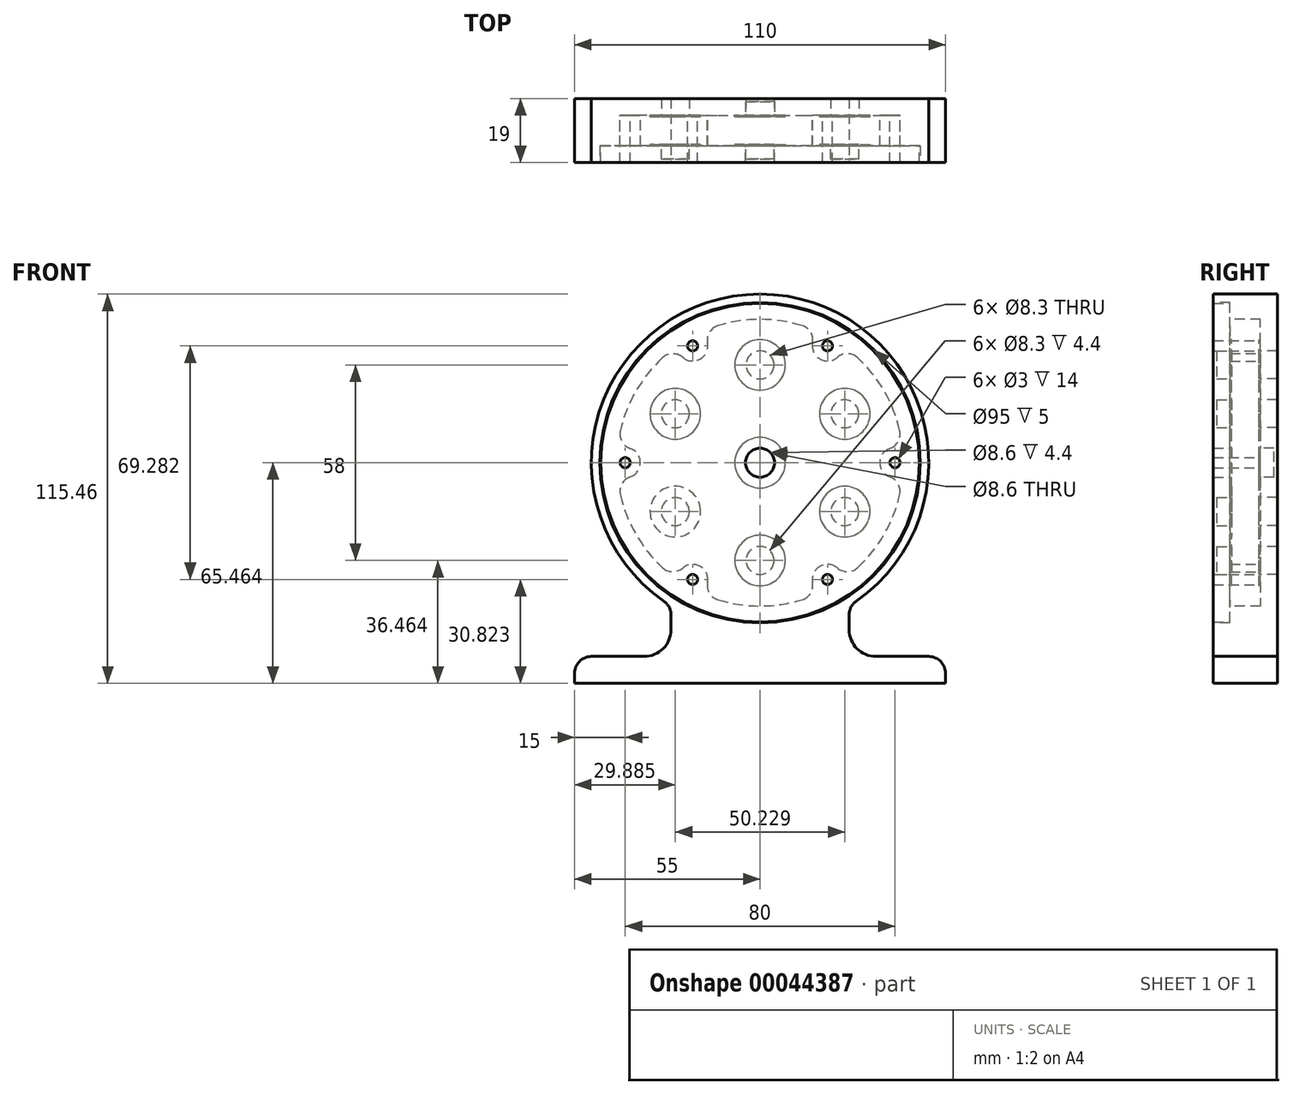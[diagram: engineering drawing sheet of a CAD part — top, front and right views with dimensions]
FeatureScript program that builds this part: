
annotation { "Feature Type Name" : "Feature", "Feature Type Description" : "" }
export const myFeature = defineFeature(function(context is Context, id is Id, definition is map)
    precondition{}
    {
        {
            var Q0;
            Q0=qCreatedBy(makeId("Front.planeOp"),FACE);
            var sketch = newSketch(context, id + "F0", { "sketchPlane" : qUnion([Q0])});
            skLineSegment(sketch, "E0", {"start": v(0, 0) * mm, "end": v(-55, 0) * mm});
            skLineSegment(sketch, "E1", {"start": v(-55, 0) * mm, "end": v(-55, 3) * mm});
            skLineSegment(sketch, "E2", {"start": v(-50, 8) * mm, "end": v(-34.4, 8) * mm});
            skLineSegment(sketch, "E3", {"start": v(-26.4, 16) * mm, "end": v(-26.4, 20.3) * mm});
            skArc(sketch, "E4", {"start": v(28.54, 24.41) * mm, "mid": v(0, 115.46) * mm, "end": v(-28.54, 24.41) * mm});
            skLineSegment(sketch, "E5", {"start": v(0, 65.46) * mm, "end": v(0, 0) * mm, "construction": true});
            skLineSegment(sketch, "E6.MirrorCS", {"start": v(0, 0) * mm, "end": v(55, 0) * mm});
            skLineSegment(sketch, "E7.MirrorCS", {"start": v(55, 0) * mm, "end": v(55, 3) * mm});
            skLineSegment(sketch, "E8.MirrorCS", {"start": v(50, 8) * mm, "end": v(34.4, 8) * mm});
            skLineSegment(sketch, "E9.MirrorCS", {"start": v(26.4, 16) * mm, "end": v(26.4, 20.3) * mm});
            skPoint(sketch, "E10.visualSharp", {"position": v(-55, 8) * mm});
            skArc(sketch, "E10.filletArc", {"start": v(-50, 8) * mm, "mid": v(-53.54, 6.54) * mm, "end": v(-55, 3) * mm});
            skPoint(sketch, "E11.visualSharp", {"position": v(55, 8) * mm});
            skArc(sketch, "E11.filletArc", {"start": v(55, 3) * mm, "mid": v(53.54, 6.54) * mm, "end": v(50, 8) * mm});
            skPoint(sketch, "E12.visualSharp", {"position": v(-26.4, 8) * mm});
            skArc(sketch, "E12.filletArc", {"start": v(-34.4, 8) * mm, "mid": v(-28.74, 10.34) * mm, "end": v(-26.4, 16) * mm});
            skPoint(sketch, "E13.visualSharp", {"position": v(26.4, 8) * mm});
            skArc(sketch, "E13.filletArc", {"start": v(26.4, 16) * mm, "mid": v(28.74, 10.34) * mm, "end": v(34.4, 8) * mm});
            skPoint(sketch, "E14.visualSharp", {"position": v(26.4, 23) * mm});
            skArc(sketch, "E14.filletArc", {"start": v(28.54, 24.41) * mm, "mid": v(26.97, 22.62) * mm, "end": v(26.4, 20.3) * mm});
            skPoint(sketch, "E15.visualSharp", {"position": v(-26.4, 23) * mm});
            skArc(sketch, "E15.filletArc", {"start": v(-26.4, 20.3) * mm, "mid": v(-26.97, 22.62) * mm, "end": v(-28.54, 24.41) * mm});
            skSolve(sketch);
        }
        {
            var Q0;
            Q0=makeQuery(id+"F0.imprint","IMPRINT",FACE,{"disambiguationData":[TD([[makeQuery(id+"F0.imprint","IMPRINT",EDGE,{"derivedFrom":sQuery(id+"F0.wireOp",EDGE,"E0")}),-1.0]])]});
            extrude(context, id + "F1", {"entities" : qUnion([Q0]), "oppositeDirection" : true, "depth" : 19 * mm});
        }
        {
            var Q0;
            Q0=makeQuery(id+"F1.opExtrude","CAP_FACE",FACE,{"disambiguationData":[OSD([sQuery(id+"F0.wireOp",EDGE,"E0"),sQuery(id+"F0.wireOp",EDGE,"E1"),sQuery(id+"F0.wireOp",EDGE,"E2"),sQuery(id+"F0.wireOp",EDGE,"E3"),sQuery(id+"F0.wireOp",EDGE,"E4"),sQuery(id+"F0.wireOp",EDGE,"E6.MirrorCS"),sQuery(id+"F0.wireOp",EDGE,"E7.MirrorCS"),sQuery(id+"F0.wireOp",EDGE,"E8.MirrorCS"),sQuery(id+"F0.wireOp",EDGE,"E9.MirrorCS"),sQuery(id+"F0.wireOp",EDGE,"E10.filletArc"),sQuery(id+"F0.wireOp",EDGE,"E11.filletArc"),sQuery(id+"F0.wireOp",EDGE,"E12.filletArc"),sQuery(id+"F0.wireOp",EDGE,"E13.filletArc"),sQuery(id+"F0.wireOp",EDGE,"E14.filletArc"),sQuery(id+"F0.wireOp",EDGE,"E15.filletArc")])],"isStart":true});
            var sketch = newSketch(context, id + "F2", { "sketchPlane" : qUnion([Q0])});
            skCircle(sketch, "E16", {"center": v(0, 65.46) * mm, "radius": 47.5 * mm});
            skSolve(sketch);
        }
        {
            var Q0;
            Q0=makeQuery(id+"F2.imprint","IMPRINT",FACE,{"disambiguationData":[TD([[makeQuery(id+"F2.imprint","IMPRINT",EDGE,{"derivedFrom":sQuery(id+"F2.wireOp",EDGE,"E16")}),1.0]])]});
            extrude(context, id + "F3", {"entities" : qUnion([Q0]), "operationType" : NewBodyOperationType.REMOVE, "oppositeDirection" : true, "depth" : 5 * mm});
        }
        {
            var Q0;
            Q0=makeQuery(id+"F3.boolean.opBoolean","COPY",FACE,{"derivedFrom":makeQuery(id+"F3.opExtrude","CAP_FACE",FACE,{"disambiguationData":[OSD([sQuery(id+"F2.wireOp",EDGE,"E16")])],"isStart":false})});
            var sketch = newSketch(context, id + "F4", { "sketchPlane" : qUnion([Q0])});
            skCircle(sketch, "E17", {"center": v(0, 65.46) * mm, "radius": 42.5 * mm});
            skSolve(sketch);
        }
        {
            var Q0;
            Q0=makeQuery(id+"F4.imprint","IMPRINT",FACE,{"disambiguationData":[TD([[makeQuery(id+"F4.imprint","IMPRINT",EDGE,{"derivedFrom":sQuery(id+"F4.wireOp",EDGE,"E17")}),1.0]])]});
            extrude(context, id + "F5", {"entities" : qUnion([Q0]), "operationType" : NewBodyOperationType.REMOVE, "oppositeDirection" : true, "depth" : 9 * mm});
        }
        {
            var Q0;
            Q0=makeQuery(id+"F5.boolean.opBoolean","COPY",FACE,{"derivedFrom":makeQuery(id+"F5.opExtrude","CAP_FACE",FACE,{"disambiguationData":[OSD([sQuery(id+"F4.wireOp",EDGE,"E17")])],"isStart":false})});
            var sketch = newSketch(context, id + "F6", { "sketchPlane" : qUnion([Q0])});
            skCircle(sketch, "E18.cCircle", {"center": v(0, 65.46) * mm, "radius": 29 * mm, "construction": true});
            skLineSegment(sketch, "E18.0", {"start": v(0, 94.46) * mm, "end": v(25.11, 79.96) * mm, "construction": true});
            skLineSegment(sketch, "E18.1", {"start": v(25.11, 79.96) * mm, "end": v(25.11, 50.96) * mm, "construction": true});
            skLineSegment(sketch, "E18.2", {"start": v(25.11, 50.96) * mm, "end": v(0, 36.46) * mm, "construction": true});
            skLineSegment(sketch, "E18.3", {"start": v(0, 36.46) * mm, "end": v(-25.11, 50.96) * mm, "construction": true});
            skLineSegment(sketch, "E18.4", {"start": v(-25.11, 50.96) * mm, "end": v(-25.11, 79.96) * mm, "construction": true});
            skLineSegment(sketch, "E18.5", {"start": v(-25.11, 79.96) * mm, "end": v(0, 94.46) * mm, "construction": true});
            skCircle(sketch, "E19", {"center": v(0, 65.46) * mm, "radius": 4.3 * mm});
            skCircle(sketch, "E20", {"center": v(0, 94.46) * mm, "radius": 4.3 * mm});
            skCircle(sketch, "E21.1.0", {"center": v(25.11, 79.96) * mm, "radius": 4.3 * mm});
            skCircle(sketch, "E21.2.0", {"center": v(25.11, 50.96) * mm, "radius": 4.3 * mm});
            skCircle(sketch, "E21.3.0", {"center": v(0, 36.46) * mm, "radius": 4.3 * mm});
            skCircle(sketch, "E21.4.0", {"center": v(-25.11, 50.96) * mm, "radius": 4.3 * mm});
            skCircle(sketch, "E21.5.0", {"center": v(-25.11, 79.96) * mm, "radius": 4.3 * mm});
            skLineSegment(sketch, "E21.anchor1", {"start": v(0, 65.46) * mm, "end": v(0, 94.46) * mm, "construction": true});
            skLineSegment(sketch, "E21.anchor2", {"start": v(0, 65.46) * mm, "end": v(-25.11, 79.96) * mm, "construction": true});
            skSolve(sketch);
        }
        {
            var Q0;
            Q0=makeQuery(id+"F6.imprint","IMPRINT",FACE,{"disambiguationData":[TD([[makeQuery(id+"F6.imprint","IMPRINT",EDGE,{"derivedFrom":sQuery(id+"F6.wireOp",EDGE,"E19")}),1.0]])]});
            extrude(context, id + "F7", {"entities" : qUnion([Q0]), "operationType" : NewBodyOperationType.REMOVE, "oppositeDirection" : true, "depth" : 4 * mm});
        }
        {
            var Q0;
            Q0=makeQuery(id+"F5.boolean.opBoolean","COPY",FACE,{"derivedFrom":makeQuery(id+"F5.opExtrude","CAP_FACE",FACE,{"disambiguationData":[OSD([sQuery(id+"F4.wireOp",EDGE,"E17")])],"isStart":false})});
            var sketch = newSketch(context, id + "F8", { "sketchPlane" : qUnion([Q0])});
            skCircle(sketch, "E22", {"center": v(0, 94.46) * mm, "radius": 4.15 * mm});
            skCircle(sketch, "E23.0", {"center": v(0, 65.46) * mm, "radius": 4.3 * mm, "construction": true});
            skLineSegment(sketch, "E24", {"start": v(0, 94.46) * mm, "end": v(0, 65.46) * mm, "construction": true});
            skCircle(sketch, "E25.1.0", {"center": v(-25.11, 79.96) * mm, "radius": 4.15 * mm});
            skCircle(sketch, "E25.2.0", {"center": v(-25.11, 50.96) * mm, "radius": 4.15 * mm});
            skCircle(sketch, "E25.3.0", {"center": v(0, 36.46) * mm, "radius": 4.15 * mm});
            skCircle(sketch, "E25.4.0", {"center": v(25.11, 50.96) * mm, "radius": 4.15 * mm});
            skCircle(sketch, "E25.5.0", {"center": v(25.11, 79.96) * mm, "radius": 4.15 * mm});
            skSolve(sketch);
        }
        {
            var Q0;
            Q0 = qSketchRegion(id + "F8", true);
            var Q1;
            Q1=makeQuery(id+"F1.opExtrude","CAP_FACE",FACE,{"disambiguationData":[OSD([sQuery(id+"F0.wireOp",EDGE,"E0"),sQuery(id+"F0.wireOp",EDGE,"E1"),sQuery(id+"F0.wireOp",EDGE,"E2"),sQuery(id+"F0.wireOp",EDGE,"E3"),sQuery(id+"F0.wireOp",EDGE,"E4"),sQuery(id+"F0.wireOp",EDGE,"E6.MirrorCS"),sQuery(id+"F0.wireOp",EDGE,"E7.MirrorCS"),sQuery(id+"F0.wireOp",EDGE,"E8.MirrorCS"),sQuery(id+"F0.wireOp",EDGE,"E9.MirrorCS"),sQuery(id+"F0.wireOp",EDGE,"E10.filletArc"),sQuery(id+"F0.wireOp",EDGE,"E11.filletArc"),sQuery(id+"F0.wireOp",EDGE,"E12.filletArc"),sQuery(id+"F0.wireOp",EDGE,"E13.filletArc"),sQuery(id+"F0.wireOp",EDGE,"E14.filletArc"),sQuery(id+"F0.wireOp",EDGE,"E15.filletArc")])],"isStart":false});
            extrude(context, id + "F9", {"entities" : qUnion([Q0]), "operationType" : NewBodyOperationType.REMOVE, "endBound" : BoundingType.UP_TO_SURFACE, "oppositeDirection" : true, "endBoundEntityFace" : qUnion([Q1]), "depth" : 25 * mm});
        }
        {
            var Q0;
            Q0=makeQuery(id+"F5.boolean.opBoolean","COPY",FACE,{"derivedFrom":makeQuery(id+"F5.opExtrude","CAP_FACE",FACE,{"disambiguationData":[OSD([sQuery(id+"F4.wireOp",EDGE,"E17")])],"isStart":false})});
            var sketch = newSketch(context, id + "F10", { "sketchPlane" : qUnion([Q0])});
            skCircle(sketch, "E26.0", {"center": v(-25.11, 79.96) * mm, "radius": 4.15 * mm});
            skCircle(sketch, "E27.0", {"center": v(0, 94.46) * mm, "radius": 4.15 * mm});
            skCircle(sketch, "E28.0", {"center": v(25.11, 79.96) * mm, "radius": 4.15 * mm});
            skCircle(sketch, "E29.0", {"center": v(25.11, 50.96) * mm, "radius": 4.15 * mm});
            skCircle(sketch, "E30.0", {"center": v(0, 36.46) * mm, "radius": 4.15 * mm});
            skCircle(sketch, "E31.0", {"center": v(-25.11, 50.96) * mm, "radius": 4.15 * mm});
            skCircle(sketch, "E32.0", {"center": v(0, 65.46) * mm, "radius": 4.3 * mm});
            skCircle(sketch, "E33", {"center": v(0, 65.46) * mm, "radius": 7.5 * mm});
            skCircle(sketch, "E34", {"center": v(0, 94.46) * mm, "radius": 7.5 * mm});
            skCircle(sketch, "E35.1.0", {"center": v(-25.11, 79.96) * mm, "radius": 7.5 * mm});
            skCircle(sketch, "E35.2.0", {"center": v(-25.11, 50.96) * mm, "radius": 7.5 * mm});
            skCircle(sketch, "E35.3.0", {"center": v(0, 36.46) * mm, "radius": 7.5 * mm});
            skCircle(sketch, "E35.4.0", {"center": v(25.11, 50.96) * mm, "radius": 7.5 * mm});
            skCircle(sketch, "E35.5.0", {"center": v(25.11, 79.96) * mm, "radius": 7.5 * mm});
            skSolve(sketch);
        }
        {
            var Q0;
            Q0 = qSketchRegion(id + "F10", true);
            extrude(context, id + "F11", {"entities" : qUnion([Q0]), "operationType" : NewBodyOperationType.ADD, "depth" : 0.4 * mm});
        }
        {
            var Q0;
            Q0=makeQuery(id+"F3.boolean.opBoolean","COPY",FACE,{"derivedFrom":makeQuery(id+"F3.opExtrude","CAP_FACE",FACE,{"disambiguationData":[OSD([sQuery(id+"F2.wireOp",EDGE,"E16")])],"isStart":false})});
            var sketch = newSketch(context, id + "F12", { "sketchPlane" : qUnion([Q0])});
            skCircle(sketch, "E36", {"center": v(0, 65.46) * mm, "radius": 47.2 * mm});
            skSolve(sketch);
        }
        {
            var Q0;
            Q0 = qSketchRegion(id + "F12", true);
            extrude(context, id + "F13", {"entities" : qUnion([Q0]), "depth" : 5 * mm});
        }
        {
            var Q0;
            Q0=makeQuery(id+"F13.opExtrude","CAP_FACE",FACE,{"disambiguationData":[OSD([sQuery(id+"F12.wireOp",EDGE,"E36")])],"isStart":true});
            var sketch = newSketch(context, id + "F14", { "sketchPlane" : qUnion([Q0])});
            skCircle(sketch, "E37.0", {"center": v(-25.11, 79.96) * mm, "radius": 4.15 * mm});
            skCircle(sketch, "E38.0", {"center": v(0, 94.46) * mm, "radius": 4.15 * mm});
            skCircle(sketch, "E39.0", {"center": v(25.11, 79.96) * mm, "radius": 4.15 * mm});
            skCircle(sketch, "E40.0", {"center": v(25.11, 50.96) * mm, "radius": 4.15 * mm});
            skCircle(sketch, "E41.0", {"center": v(0, 36.46) * mm, "radius": 4.15 * mm});
            skCircle(sketch, "E42.0", {"center": v(-25.11, 50.96) * mm, "radius": 4.15 * mm});
            skSolve(sketch);
        }
        {
            var Q0;
            Q0=makeQuery(id+"F14.imprint","IMPRINT",FACE,{"disambiguationData":[TD([[makeQuery(id+"F14.imprint","IMPRINT",EDGE,{"derivedFrom":sQuery(id+"F14.wireOp",EDGE,"E37.0")}),1.0]])]});
            var Q1;
            Q1=makeQuery(id+"F14.imprint","IMPRINT",FACE,{"disambiguationData":[TD([[makeQuery(id+"F14.imprint","IMPRINT",EDGE,{"derivedFrom":sQuery(id+"F14.wireOp",EDGE,"E38.0")}),1.0]])]});
            var Q2;
            Q2=makeQuery(id+"F14.imprint","IMPRINT",FACE,{"disambiguationData":[TD([[makeQuery(id+"F14.imprint","IMPRINT",EDGE,{"derivedFrom":sQuery(id+"F14.wireOp",EDGE,"E39.0")}),1.0]])]});
            var Q3;
            Q3=makeQuery(id+"F14.imprint","IMPRINT",FACE,{"disambiguationData":[TD([[makeQuery(id+"F14.imprint","IMPRINT",EDGE,{"derivedFrom":sQuery(id+"F14.wireOp",EDGE,"E40.0")}),1.0]])]});
            var Q4;
            Q4=makeQuery(id+"F14.imprint","IMPRINT",FACE,{"disambiguationData":[TD([[makeQuery(id+"F14.imprint","IMPRINT",EDGE,{"derivedFrom":sQuery(id+"F14.wireOp",EDGE,"E41.0")}),1.0]])]});
            var Q5;
            Q5=makeQuery(id+"F14.imprint","IMPRINT",FACE,{"disambiguationData":[TD([[makeQuery(id+"F14.imprint","IMPRINT",EDGE,{"derivedFrom":sQuery(id+"F14.wireOp",EDGE,"E42.0")}),1.0]])]});
            extrude(context, id + "F15", {"entities" : qUnion([Q0, Q1, Q2, Q3, Q4, Q5]), "operationType" : NewBodyOperationType.REMOVE, "oppositeDirection" : true, "depth" : 4 * mm});
        }
        {
            var Q0;
            Q0=makeQuery(id+"F13.opExtrude","CAP_FACE",FACE,{"disambiguationData":[OSD([sQuery(id+"F12.wireOp",EDGE,"E36")])],"isStart":true});
            var sketch = newSketch(context, id + "F16", { "sketchPlane" : qUnion([Q0])});
            skCircle(sketch, "E43.0", {"center": v(0, 65.46) * mm, "radius": 4.3 * mm});
            skSolve(sketch);
        }
        {
            var Q0;
            Q0=makeQuery(id+"F16.imprint","IMPRINT",FACE,{"disambiguationData":[TD([[makeQuery(id+"F16.imprint","IMPRINT",EDGE,{"derivedFrom":sQuery(id+"F16.wireOp",EDGE,"E43.0")}),1.0]])]});
            extrude(context, id + "F17", {"entities" : qUnion([Q0]), "operationType" : NewBodyOperationType.REMOVE, "endBound" : BoundingType.UP_TO_NEXT, "oppositeDirection" : true, "depth" : 25 * mm});
        }
        {
            var Q0;
            Q0=makeQuery(id+"F13.opExtrude","CAP_FACE",FACE,{"disambiguationData":[OSD([sQuery(id+"F12.wireOp",EDGE,"E36")])],"isStart":true});
            var sketch = newSketch(context, id + "F18", { "sketchPlane" : qUnion([Q0])});
            skCircle(sketch, "E44.0", {"center": v(25.11, 50.96) * mm, "radius": 4.15 * mm});
            skCircle(sketch, "E45.0", {"center": v(0, 36.46) * mm, "radius": 4.15 * mm});
            skCircle(sketch, "E46.0", {"center": v(-25.11, 50.96) * mm, "radius": 4.15 * mm});
            skCircle(sketch, "E47.0", {"center": v(-25.11, 79.96) * mm, "radius": 4.15 * mm});
            skCircle(sketch, "E48.0", {"center": v(0, 94.46) * mm, "radius": 4.15 * mm});
            skCircle(sketch, "E49.0", {"center": v(25.11, 79.96) * mm, "radius": 4.15 * mm});
            skCircle(sketch, "E50.0", {"center": v(0, 65.46) * mm, "radius": 4.3 * mm});
            skCircle(sketch, "E51", {"center": v(0, 65.46) * mm, "radius": 7.5 * mm});
            skCircle(sketch, "E52", {"center": v(0, 36.46) * mm, "radius": 7.5 * mm});
            skCircle(sketch, "E53.1.0", {"center": v(25.11, 50.96) * mm, "radius": 7.5 * mm});
            skCircle(sketch, "E53.2.0", {"center": v(25.11, 79.96) * mm, "radius": 7.5 * mm});
            skCircle(sketch, "E53.3.0", {"center": v(0, 94.46) * mm, "radius": 7.5 * mm});
            skCircle(sketch, "E53.4.0", {"center": v(-25.11, 79.96) * mm, "radius": 7.5 * mm});
            skCircle(sketch, "E53.5.0", {"center": v(-25.11, 50.96) * mm, "radius": 7.5 * mm});
            skSolve(sketch);
        }
        {
            var Q0;
            Q0 = qSketchRegion(id + "F18", true);
            extrude(context, id + "F19", {"entities" : qUnion([Q0]), "operationType" : NewBodyOperationType.ADD, "depth" : .4 * mm});
        }
        {
            var Q0;
            Q0=makeQuery(id+"F13.opExtrude","CAP_FACE",FACE,{"disambiguationData":[OSD([sQuery(id+"F12.wireOp",EDGE,"E36")])],"isStart":true});
            var sketch = newSketch(context, id + "F20", { "sketchPlane" : qUnion([Q0])});
            skLineSegment(sketch, "E54", {"start": v(0, 65.46) * mm, "end": v(0, 36.46) * mm, "construction": true});
            skLineSegment(sketch, "E55", {"start": v(0, 65.46) * mm, "end": v(23.6, 24.59) * mm, "construction": true});
            skCircle(sketch, "E56", {"center": v(20, 30.82) * mm, "radius": 1.5 * mm});
            skCircle(sketch, "E57.1.0", {"center": v(40, 65.46) * mm, "radius": 1.5 * mm});
            skCircle(sketch, "E57.2.0", {"center": v(20, 100.1) * mm, "radius": 1.5 * mm});
            skCircle(sketch, "E57.3.0", {"center": v(-20, 100.1) * mm, "radius": 1.5 * mm});
            skCircle(sketch, "E57.4.0", {"center": v(-40, 65.46) * mm, "radius": 1.5 * mm});
            skCircle(sketch, "E57.5.0", {"center": v(-20, 30.82) * mm, "radius": 1.5 * mm});
            skPoint(sketch, "E57.center", {"position": v(0, 65.46) * mm});
            skSolve(sketch);
        }
        {
            var Q0;
            Q0 = qSketchRegion(id + "F20", true);
            extrude(context, id + "F21", {"entities" : qUnion([Q0]), "operationType" : NewBodyOperationType.REMOVE, "endBound" : BoundingType.UP_TO_NEXT, "oppositeDirection" : true, "depth" : 25 * mm});
        }
        {
            var Q0;
            Q0=makeQuery(id+"F5.boolean.opBoolean","COPY",FACE,{"derivedFrom":makeQuery(id+"F5.opExtrude","CAP_FACE",FACE,{"disambiguationData":[OSD([sQuery(id+"F4.wireOp",EDGE,"E17")])],"isStart":false})});
            var sketch = newSketch(context, id + "F22", { "sketchPlane" : qUnion([Q0])});
            skCircle(sketch, "E58.0", {"center": v(-20, 100.1) * mm, "radius": 1.5 * mm});
            skArc(sketch, "E59", {"start": v(-22.94, 96.7) * mm, "mid": v(-17.75, 96.2) * mm, "end": v(-15.58, 100.95) * mm});
            skPoint(sketch, "E60.visualSharp", {"position": v(-24.5, 100.2) * mm});
            skArc(sketch, "E60.filletArc", {"start": v(-22.94, 96.7) * mm, "mid": v(-25.96, 97.79) * mm, "end": v(-28.94, 96.59) * mm});
            skPoint(sketch, "E61.visualSharp", {"position": v(-17.83, 104.05) * mm});
            skArc(sketch, "E61.filletArc", {"start": v(-12.48, 106.1) * mm, "mid": v(-15.01, 104.11) * mm, "end": v(-15.58, 100.95) * mm});
            skArc(sketch, "E62.0", {"start": v(-12.48, 106.1) * mm, "mid": v(-21.25, 102.27) * mm, "end": v(-28.94, 96.59) * mm});
            skArc(sketch, "E63.1.0", {"start": v(-38.52, 61.22) * mm, "mid": v(-35.5, 65.46) * mm, "end": v(-38.52, 69.71) * mm});
            skArc(sketch, "E63.1.1", {"start": v(-38.52, 61.22) * mm, "mid": v(-40.98, 59.14) * mm, "end": v(-41.42, 55.96) * mm});
            skArc(sketch, "E63.1.2", {"start": v(-41.42, 74.97) * mm, "mid": v(-42.5, 65.46) * mm, "end": v(-41.42, 55.96) * mm});
            skArc(sketch, "E63.1.3", {"start": v(-41.42, 74.97) * mm, "mid": v(-40.98, 71.79) * mm, "end": v(-38.52, 69.71) * mm});
            skCircle(sketch, "E63.1.4", {"center": v(-40, 65.46) * mm, "radius": 1.5 * mm});
            skArc(sketch, "E63.2.0", {"start": v(-15.58, 29.98) * mm, "mid": v(-17.75, 34.72) * mm, "end": v(-22.94, 34.23) * mm});
            skArc(sketch, "E63.2.1", {"start": v(-15.58, 29.98) * mm, "mid": v(-15.01, 26.82) * mm, "end": v(-12.48, 24.84) * mm});
            skArc(sketch, "E63.2.2", {"start": v(-28.94, 34.34) * mm, "mid": v(-21.25, 28.66) * mm, "end": v(-12.48, 24.84) * mm});
            skArc(sketch, "E63.2.3", {"start": v(-28.94, 34.34) * mm, "mid": v(-25.96, 33.14) * mm, "end": v(-22.94, 34.23) * mm});
            skCircle(sketch, "E63.2.4", {"center": v(-20, 30.82) * mm, "radius": 1.5 * mm});
            skArc(sketch, "E63.3.0", {"start": v(22.94, 34.23) * mm, "mid": v(17.75, 34.72) * mm, "end": v(15.58, 29.98) * mm});
            skArc(sketch, "E63.3.1", {"start": v(22.94, 34.23) * mm, "mid": v(25.96, 33.14) * mm, "end": v(28.94, 34.34) * mm});
            skArc(sketch, "E63.3.2", {"start": v(12.48, 24.84) * mm, "mid": v(21.25, 28.66) * mm, "end": v(28.94, 34.34) * mm});
            skArc(sketch, "E63.3.3", {"start": v(12.48, 24.84) * mm, "mid": v(15.01, 26.82) * mm, "end": v(15.58, 29.98) * mm});
            skCircle(sketch, "E63.3.4", {"center": v(20, 30.82) * mm, "radius": 1.5 * mm});
            skArc(sketch, "E63.4.0", {"start": v(38.52, 69.71) * mm, "mid": v(35.5, 65.46) * mm, "end": v(38.52, 61.22) * mm});
            skArc(sketch, "E63.4.1", {"start": v(38.52, 69.71) * mm, "mid": v(40.98, 71.79) * mm, "end": v(41.42, 74.97) * mm});
            skArc(sketch, "E63.4.2", {"start": v(41.42, 55.96) * mm, "mid": v(42.5, 65.46) * mm, "end": v(41.42, 74.97) * mm});
            skArc(sketch, "E63.4.3", {"start": v(41.42, 55.96) * mm, "mid": v(40.98, 59.14) * mm, "end": v(38.52, 61.22) * mm});
            skCircle(sketch, "E63.4.4", {"center": v(40, 65.46) * mm, "radius": 1.5 * mm});
            skArc(sketch, "E63.5.0", {"start": v(15.58, 100.95) * mm, "mid": v(17.75, 96.2) * mm, "end": v(22.94, 96.7) * mm});
            skArc(sketch, "E63.5.1", {"start": v(15.58, 100.95) * mm, "mid": v(15.01, 104.11) * mm, "end": v(12.48, 106.1) * mm});
            skArc(sketch, "E63.5.2", {"start": v(28.94, 96.59) * mm, "mid": v(21.25, 102.27) * mm, "end": v(12.48, 106.1) * mm});
            skArc(sketch, "E63.5.3", {"start": v(28.94, 96.59) * mm, "mid": v(25.96, 97.79) * mm, "end": v(22.94, 96.7) * mm});
            skCircle(sketch, "E63.5.4", {"center": v(20, 100.1) * mm, "radius": 1.5 * mm});
            skSolve(sketch);
        }
        {
            var Q0;
            Q0 = qSketchRegion(id + "F22", true);
            extrude(context, id + "F23", {"entities" : qUnion([Q0]), "operationType" : NewBodyOperationType.ADD, "depth" : 9 * mm});
        }
    });
